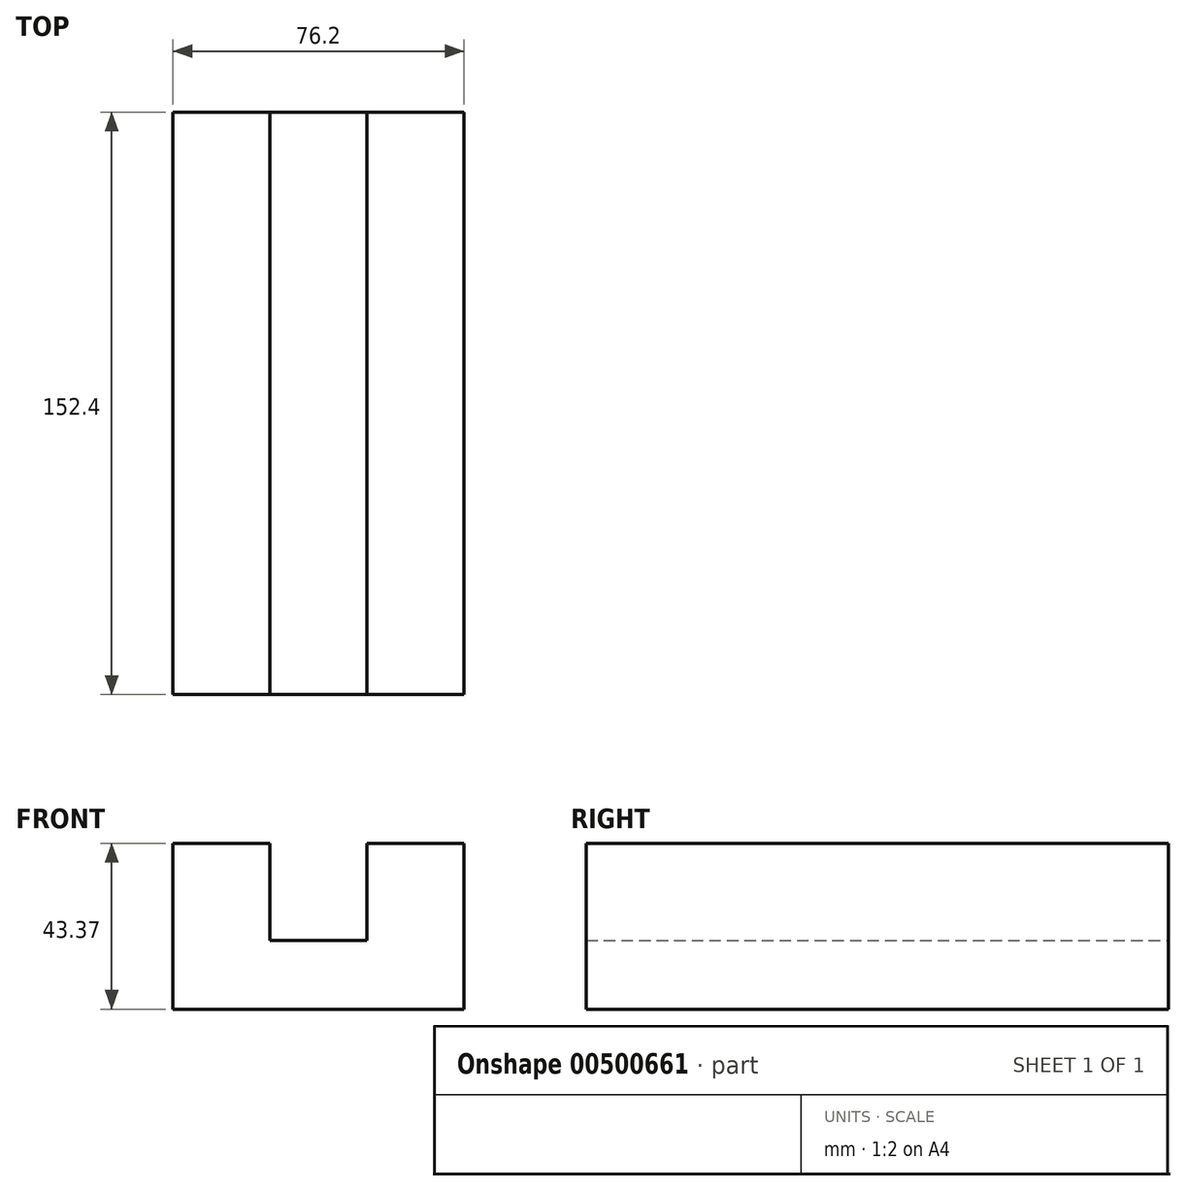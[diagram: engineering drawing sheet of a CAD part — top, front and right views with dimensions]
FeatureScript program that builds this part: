
annotation { "Feature Type Name" : "Feature", "Feature Type Description" : "" }
export const myFeature = defineFeature(function(context is Context, id is Id, definition is map)
    precondition{}
    {
        {
            var Q0;
            Q0=qCreatedBy(makeId("Front.planeOp"),FACE);
            var sketch = newSketch(context, id + "F0", { "sketchPlane" : qUnion([Q0])});
            skLineSegment(sketch, "E0", {"start": v(-29.23, 26.15) * mm, "end": v(-29.23, -17.22) * mm});
            skLineSegment(sketch, "E1", {"start": v(-29.23, -17.22) * mm, "end": v(46.97, -17.22) * mm});
            skLineSegment(sketch, "E2", {"start": v(46.97, -17.22) * mm, "end": v(46.97, 26.15) * mm});
            skLineSegment(sketch, "E3", {"start": v(46.97, 26.15) * mm, "end": v(21.57, 26.15) * mm});
            skLineSegment(sketch, "E4", {"start": v(21.57, 26.15) * mm, "end": v(21.57, 0.75) * mm});
            skLineSegment(sketch, "E5", {"start": v(21.57, 0.75) * mm, "end": v(-3.83, 0.75) * mm});
            skLineSegment(sketch, "E6", {"start": v(-3.83, 0.75) * mm, "end": v(-3.83, 26.15) * mm});
            skLineSegment(sketch, "E7", {"start": v(-3.83, 26.15) * mm, "end": v(-29.23, 26.15) * mm});
            skSolve(sketch);
        }
        {
            var Q0;
            Q0 = qSketchRegion(id + "F0", true);
            extrude(context, id + "F1", {"entities" : qUnion([Q0]), "depth" : 152.4 * mm});
        }
    });
